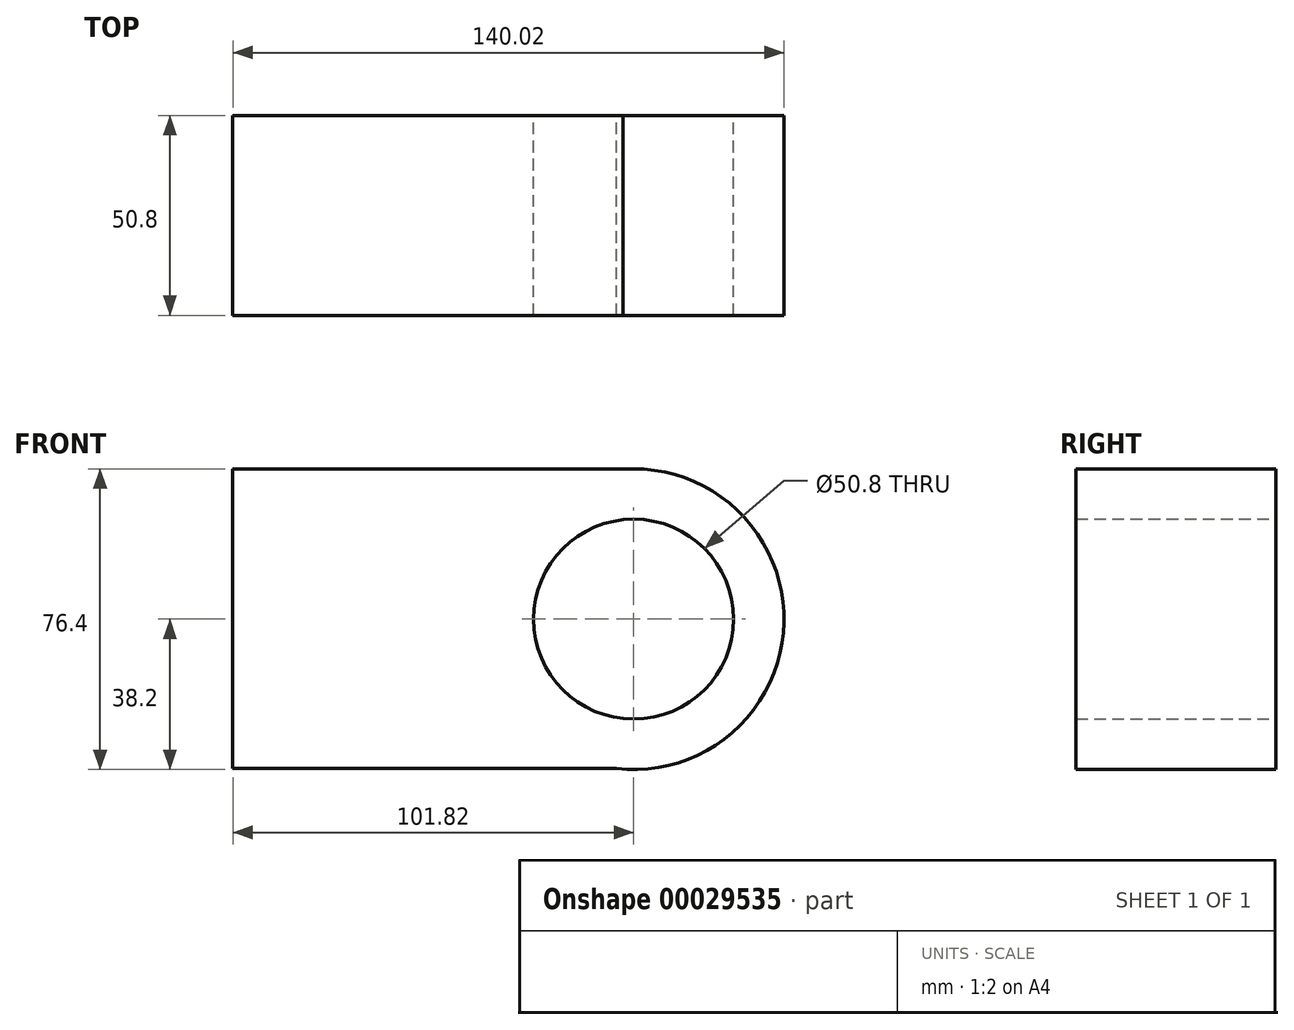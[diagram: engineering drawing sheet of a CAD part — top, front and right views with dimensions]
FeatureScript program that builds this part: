
annotation { "Feature Type Name" : "Feature", "Feature Type Description" : "" }
export const myFeature = defineFeature(function(context is Context, id is Id, definition is map)
    precondition{}
    {
        {
            var Q0;
            Q0=qCreatedBy(makeId("Front.planeOp"),FACE);
            var sketch = newSketch(context, id + "F0", { "sketchPlane" : qUnion([Q0])});
            skCircle(sketch, "E0", {"center": v(0, 0) * mm, "radius": 25.4 * mm});
            skLineSegment(sketch, "E1.bottom", {"start": v(0, 38.1) * mm, "end": v(-101.82, 38.1) * mm});
            skLineSegment(sketch, "E1.top", {"start": v(0, -37.95) * mm, "end": v(-101.82, -37.95) * mm});
            skLineSegment(sketch, "E1.right", {"start": v(-101.82, 38.1) * mm, "end": v(-101.82, -37.95) * mm});
            skArc(sketch, "E2", {"start": v(-4.37, -37.95) * mm, "mid": v(38.19, -0.83) * mm, "end": v(-2.73, 38.1) * mm});
            skSolve(sketch);
        }
        {
            var Q0;
            Q0=makeQuery(id+"F0.imprint","IMPRINT",FACE,{"disambiguationData":[TD([[makeQuery(id+"F0.imprint","IMPRINT",EDGE,{"derivedFrom":sQuery(id+"F0.wireOp",EDGE,"E0")}),-1.0]])]});
            extrude(context, id + "F1", {"entities" : qUnion([Q0]), "depth" : 50.8 * mm});
        }
    });
